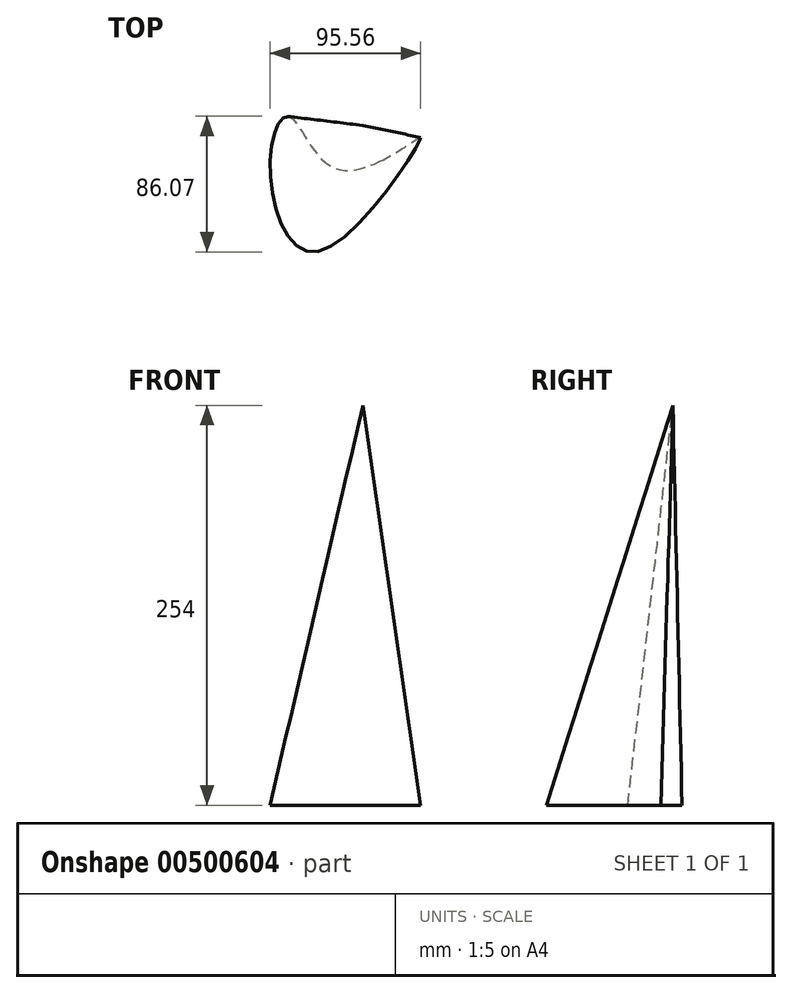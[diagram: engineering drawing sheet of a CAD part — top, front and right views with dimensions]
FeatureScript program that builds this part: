
annotation { "Feature Type Name" : "Feature", "Feature Type Description" : "" }
export const myFeature = defineFeature(function(context is Context, id is Id, definition is map)
    precondition{}
    {
        {
            var Q0;
            Q0=qCreatedBy(makeId("Top.planeOp"),FACE);
            var sketch = newSketch(context, id + "F0", { "sketchPlane" : qUnion([Q0])});
            skFitSpline(sketch, "E0", {"points": [v(-57.8, 7.47) * mm, v(-45.64, 39.35) * mm, v(-13.73, 5.65) * mm, v(37.17, 26.07) * mm, v(37.75, 25.78) * mm, v(-27.17, -46.13) * mm, v(-57.8, 7.47) * mm]});
            skSolve(sketch);
        }
        {
            var Q0;
            Q0=qCreatedBy(makeId("Top.planeOp"),FACE);
            cPlane(context, id + "F1", {"entities" : qUnion([Q0]), "cplaneType" : CPlaneType.OFFSET, "offset" : 254 * mm, "width" : 152.4 * mm, "height" : 152.4 * mm});
        }
        {
            var Q0;
            Q0=qCreatedBy(id+"F1.planeOp",FACE);
            var sketch = newSketch(context, id + "F2", { "sketchPlane" : qUnion([Q0])});
            skPoint(sketch, "E1", {"position": v(1.1, 33.77) * mm});
            skSolve(sketch);
        }
        {
            var Q0;
            Q0=makeQuery(id+"F0.imprint","IMPRINT",FACE,{"disambiguationData":[TD([[makeQuery(id+"F0.imprint","IMPRINT",EDGE,{"derivedFrom":sQuery(id+"F0.wireOp",EDGE,"E0")}),-1.0]])]});
            var Q1;
            Q1=sQuery(id+"F2.wireOp",VERTEX,"E1");
            loft(context, id + "F3", {"sheetProfilesArray" : [{ "sheetProfileEntities" : qUnion([Q0]) }, { "sheetProfileEntities" : qUnion([Q1]) }]});
        }
    });
